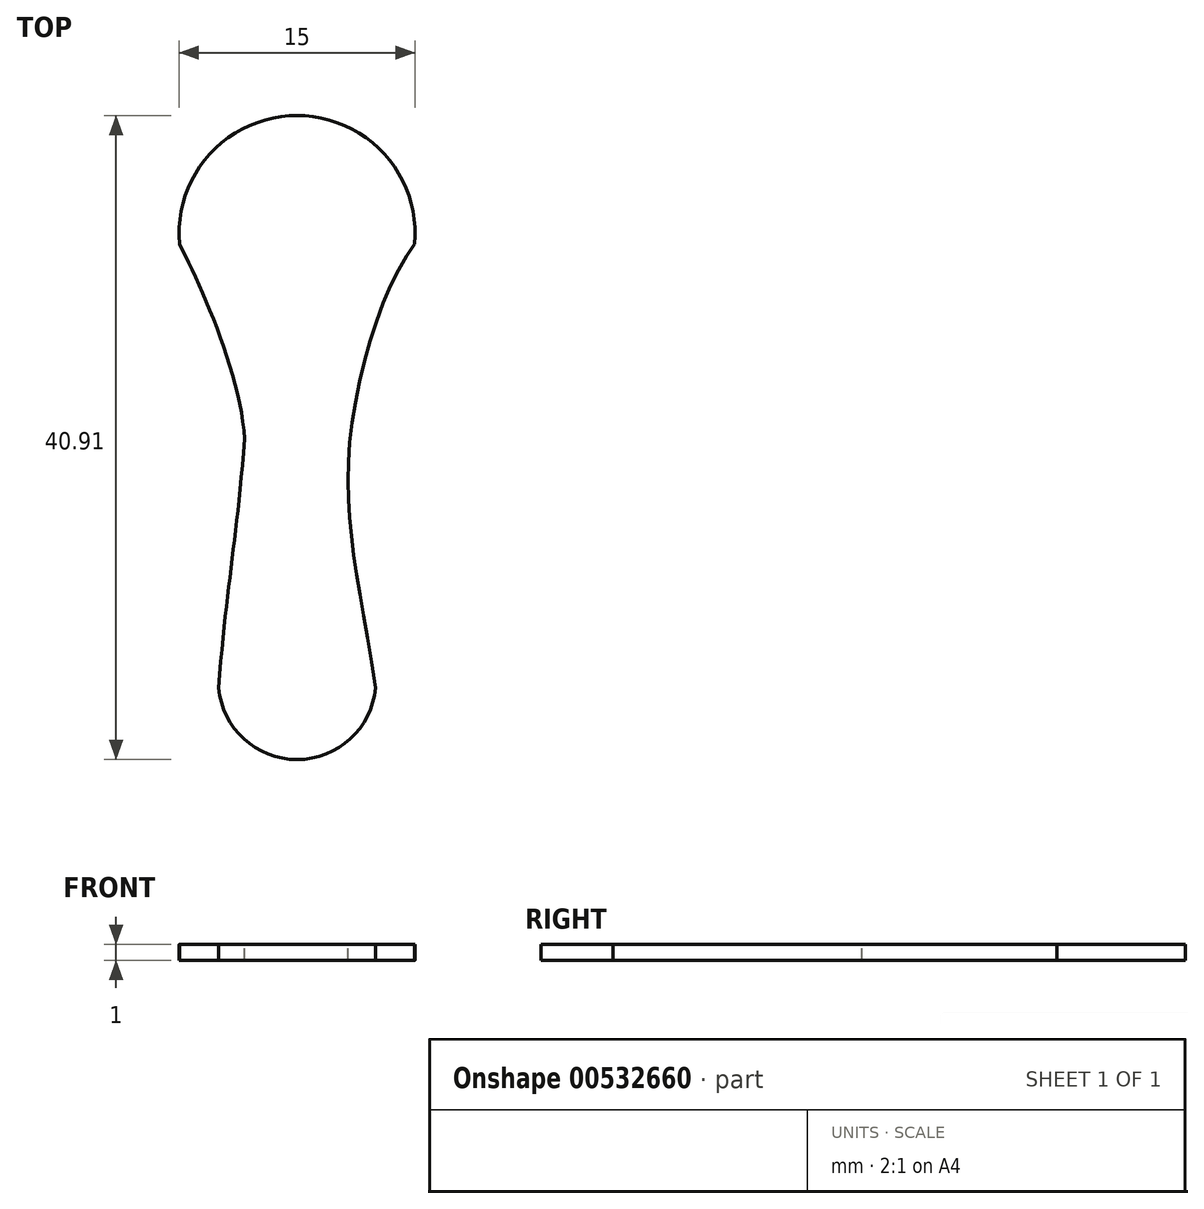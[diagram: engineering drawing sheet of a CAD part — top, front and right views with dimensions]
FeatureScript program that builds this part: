
annotation { "Feature Type Name" : "Feature", "Feature Type Description" : "" }
export const myFeature = defineFeature(function(context is Context, id is Id, definition is map)
    precondition{}
    {
        {
            var Q0;
            Q0=qCreatedBy(makeId("Top.planeOp"),FACE);
            var sketch = newSketch(context, id + "F0", { "sketchPlane" : qUnion([Q0])});
            skCircle(sketch, "E0", {"center": v(0, 0) * mm, "radius": 7.5 * mm});
            skCircle(sketch, "E1", {"center": v(0, -28.4) * mm, "radius": 5 * mm});
            skLineSegment(sketch, "E2", {"start": v(7.47, -0.66) * mm, "end": v(4.98, -28.85) * mm});
            skLineSegment(sketch, "E3", {"start": v(-7.47, -0.66) * mm, "end": v(-4.98, -28.85) * mm});
            skSolve(sketch);
        }
        {
            var Q0;
            {var subQ0=sQuery(id+"F0.wireOp",EDGE,"E0");var subQ1=makeQuery(id+"F0.imprint","INTERSECT",VERTEX,{"derivedFrom":[subQ0,sQuery(id+"F0.wireOp",EDGE,"E2")]});Q0=makeQuery(id+"F0.imprint","IMPRINT",FACE,{"disambiguationData":[TD([[makeQuery(id+"F0.imprint","IMPRINT",EDGE,{"disambiguationData":[TD([[subQ1,1.0]])],"derivedFrom":subQ0}),1.0]])]});}
            var Q1;
            {var subQ0=sQuery(id+"F0.wireOp",EDGE,"E2");Q1=makeQuery(id+"F0.imprint","IMPRINT",FACE,{"disambiguationData":[TD([[makeQuery(id+"F0.imprint","IMPRINT",EDGE,{"derivedFrom":subQ0}),-1.0]])]});}
            var Q2;
            {var subQ0=sQuery(id+"F0.wireOp",EDGE,"E1");var subQ1=makeQuery(id+"F0.imprint","INTERSECT",VERTEX,{"derivedFrom":[subQ0,sQuery(id+"F0.wireOp",EDGE,"E2")]});Q2=makeQuery(id+"F0.imprint","IMPRINT",FACE,{"disambiguationData":[TD([[makeQuery(id+"F0.imprint","IMPRINT",EDGE,{"disambiguationData":[TD([[subQ1,1.0]])],"derivedFrom":subQ0}),1.0]])]});}
            extrude(context, id + "F1", {"entities" : qUnion([Q0, Q1, Q2]), "depth" : 1 * mm, "offsetDistance" : 25 * mm});
        }
        {
            var Q0;
            Q0=makeQuery(id+"F1.opExtrude","CAP_FACE",FACE,{"disambiguationData":[OSD([sQuery(id+"F0.wireOp",EDGE,"E0"),sQuery(id+"F0.wireOp",EDGE,"E1"),sQuery(id+"F0.wireOp",EDGE,"E2"),sQuery(id+"F0.wireOp",EDGE,"E3")])],"isStart":false});
            var sketch = newSketch(context, id + "F2", { "sketchPlane" : qUnion([Q0])});
            skFitSpline(sketch, "E4", {"points": [v(7.47, -0.66) * mm, v(3.34, -13.35) * mm, v(4.98, -28.85) * mm], "startDerivative": vector(-12.31, -15.76) * mm, "endDerivative": vector(5.9, -38.82) * mm});
            skFitSpline(sketch, "E5", {"points": [v(-7.47, -0.66) * mm, v(-3.34, -13.04) * mm], "startDerivative": vector(4.06, -7.93) * mm, "endDerivative": vector(0.7, -12.43) * mm});
            skFitSpline(sketch, "E6", {"points": [v(-3.34, -13.04) * mm, v(-4.98, -28.85) * mm], "startDerivative": vector(-1.57, -20.25) * mm, "endDerivative": vector(-1.57, -20.25) * mm});
            skSolve(sketch);
        }
        {
            var Q0;
            Q0=makeQuery(id+"F2.imprint","IMPRINT",FACE,{"disambiguationData":[TD([[makeQuery(id+"F2.imprint","IMPRINT",EDGE,{"derivedFrom":sQuery(id+"F2.wireOp",EDGE,"E4")}),1.0]])]});
            var Q1;
            Q1=makeQuery(id+"F2.imprint","IMPRINT",FACE,{"disambiguationData":[TD([[makeQuery(id+"F2.imprint","IMPRINT",EDGE,{"derivedFrom":sQuery(id+"F2.wireOp",EDGE,"E5")}),-1.0]])]});
            extrude(context, id + "F3", {"entities" : qUnion([Q0, Q1]), "operationType" : NewBodyOperationType.REMOVE, "endBound" : BoundingType.THROUGH_ALL, "oppositeDirection" : true, "depth" : 25 * mm, "offsetDistance" : 25 * mm});
        }
    });
